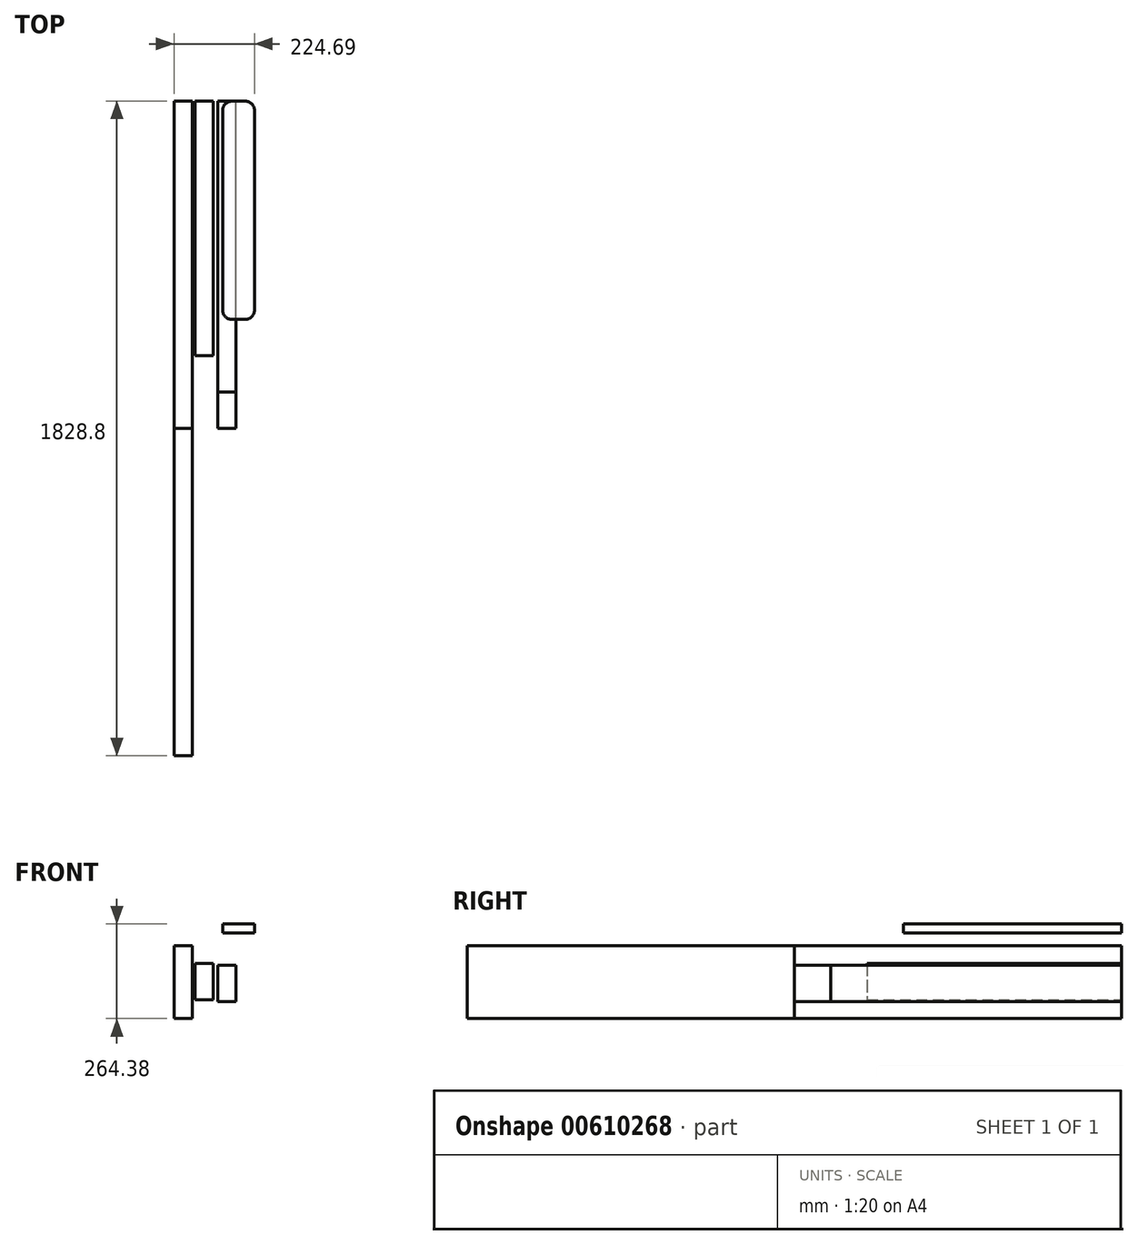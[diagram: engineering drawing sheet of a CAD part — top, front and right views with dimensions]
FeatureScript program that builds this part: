
annotation { "Feature Type Name" : "Feature", "Feature Type Description" : "" }
export const myFeature = defineFeature(function(context is Context, id is Id, definition is map)
    precondition{}
    {
        {
            var Q0;
            Q0=qCreatedBy(makeId("Front.planeOp"),FACE);
            var sketch = newSketch(context, id + "F0", { "sketchPlane" : qUnion([Q0])});
            skLineSegment(sketch, "E0.bottom", {"start": v(-25.4, 50.8) * mm, "end": v(25.4, 50.8) * mm});
            skLineSegment(sketch, "E0.top", {"start": v(-25.4, -50.8) * mm, "end": v(25.4, -50.8) * mm});
            skLineSegment(sketch, "E0.left", {"start": v(-25.4, 50.8) * mm, "end": v(-25.4, -50.8) * mm});
            skLineSegment(sketch, "E0.right", {"start": v(25.4, 50.8) * mm, "end": v(25.4, -50.8) * mm});
            skSolve(sketch);
        }
        {
            var Q0;
            Q0 = qSketchRegion(id + "F0", true);
            extrude(context, id + "F1", {"entities" : qUnion([Q0]), "depth" : 711.2 * mm, "offsetDistance" : 25.4 * mm});
        }
        {
            var Q0;
            Q0=qCreatedBy(makeId("Front.planeOp"),FACE);
            var sketch = newSketch(context, id + "F2", { "sketchPlane" : qUnion([Q0])});
            skLineSegment(sketch, "E1.bottom", {"start": v(38.05, 45.13) * mm, "end": v(88.85, 45.13) * mm});
            skLineSegment(sketch, "E1.top", {"start": v(38.05, -56.47) * mm, "end": v(88.85, -56.47) * mm});
            skLineSegment(sketch, "E1.left", {"start": v(38.05, 45.13) * mm, "end": v(38.05, -56.47) * mm});
            skLineSegment(sketch, "E1.right", {"start": v(88.85, 45.13) * mm, "end": v(88.85, -56.47) * mm});
            skSolve(sketch);
        }
        {
            var Q0;
            Q0 = qSketchRegion(id + "F2", true);
            extrude(context, id + "F3", {"entities" : qUnion([Q0]), "depth" : 812.8 * mm, "offsetDistance" : 25.4 * mm});
        }
        {
            var Q0;
            Q0=qCreatedBy(makeId("Front.planeOp"),FACE);
            var sketch = newSketch(context, id + "F4", { "sketchPlane" : qUnion([Q0])});
            skLineSegment(sketch, "E2.bottom", {"start": v(-83.91, 99.27) * mm, "end": v(-33.11, 99.27) * mm});
            skLineSegment(sketch, "E2.top", {"start": v(-83.91, -103.93) * mm, "end": v(-33.11, -103.93) * mm});
            skLineSegment(sketch, "E2.left", {"start": v(-83.91, 99.27) * mm, "end": v(-83.91, -103.93) * mm});
            skLineSegment(sketch, "E2.right", {"start": v(-33.11, 99.27) * mm, "end": v(-33.11, -103.93) * mm});
            skSolve(sketch);
        }
        {
            var Q0;
            Q0 = qSketchRegion(id + "F4", true);
            extrude(context, id + "F5", {"entities" : qUnion([Q0]), "depth" : 914.4 * mm, "offsetDistance" : 25.4 * mm});
        }
        {
            var Q0;
            Q0 = qSketchRegion(id + "F4", true);
            extrude(context, id + "F6", {"entities" : qUnion([Q0]), "depth" : 1828.8 * mm, "offsetDistance" : 25.4 * mm});
        }
        {
            var Q0;
            Q0 = qSketchRegion(id + "F2", true);
            extrude(context, id + "F7", {"entities" : qUnion([Q0]), "depth" : 914.4 * mm, "offsetDistance" : 25.4 * mm});
        }
        {
            var Q0;
            Q0=qCreatedBy(makeId("Front.planeOp"),FACE);
            var sketch = newSketch(context, id + "F8", { "sketchPlane" : qUnion([Q0])});
            skLineSegment(sketch, "E3.bottom", {"start": v(140.78, 160.45) * mm, "end": v(51.88, 160.45) * mm});
            skLineSegment(sketch, "E3.top", {"start": v(140.78, 135.05) * mm, "end": v(51.88, 135.05) * mm});
            skLineSegment(sketch, "E3.left", {"start": v(140.78, 160.45) * mm, "end": v(140.78, 135.05) * mm});
            skLineSegment(sketch, "E3.right", {"start": v(51.88, 160.45) * mm, "end": v(51.88, 135.05) * mm});
            skSolve(sketch);
        }
        {
            var Q0;
            Q0 = qSketchRegion(id + "F8", true);
            extrude(context, id + "F9", {"entities" : qUnion([Q0]), "depth" : 609.6 * mm, "offsetDistance" : 25.4 * mm});
        }
        {
            var Q0;
            Q0=makeQuery(id+"F9.opExtrude","CAP_EDGE",EDGE,{"disambiguationData":[OSD([sQuery(id+"F8.wireOp",EDGE,"E3.left")])],"isStart":true});
            var Q1;
            Q1=makeQuery(id+"F9.opExtrude","CAP_EDGE",EDGE,{"disambiguationData":[OSD([sQuery(id+"F8.wireOp",EDGE,"E3.right")])],"isStart":true});
            var Q2;
            Q2=makeQuery(id+"F9.opExtrude","CAP_EDGE",EDGE,{"disambiguationData":[OSD([sQuery(id+"F8.wireOp",EDGE,"E3.right")])],"isStart":false});
            var Q3;
            Q3=makeQuery(id+"F9.opExtrude","CAP_EDGE",EDGE,{"disambiguationData":[OSD([sQuery(id+"F8.wireOp",EDGE,"E3.left")])],"isStart":false});
            fillet(context, id + "F10", {"entities" : qUnion([Q0, Q1, Q2, Q3]), "radius" : 25.4 * mm, "tangentPropagation" : true, "allowEdgeOverflow" : false});
        }
    });
